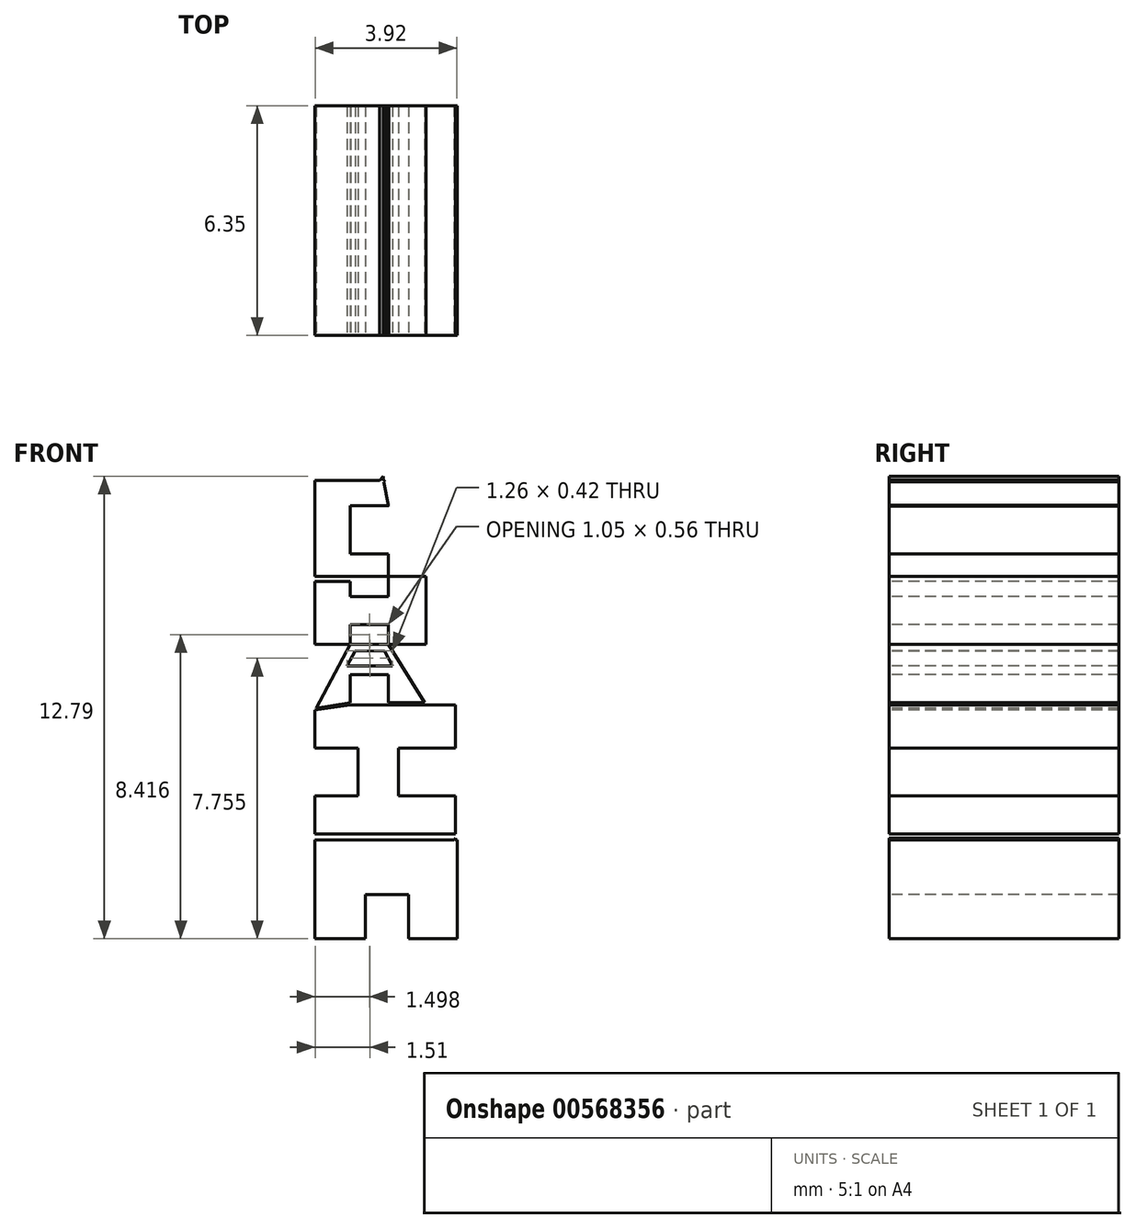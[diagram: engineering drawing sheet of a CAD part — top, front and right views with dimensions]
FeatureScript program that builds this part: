
annotation { "Feature Type Name" : "Feature", "Feature Type Description" : "" }
export const myFeature = defineFeature(function(context is Context, id is Id, definition is map)
    precondition{}
    {
        {
            var Q0;
            Q0=qCreatedBy(makeId("Front.planeOp"),FACE);
            var sketch = newSketch(context, id + "F0", { "sketchPlane" : qUnion([Q0])});
            skLineSegment(sketch, "E0", {"start": v(0, 0) * mm, "end": v(0, 25.4) * mm});
            skLineSegment(sketch, "E1", {"start": v(0, 25.4) * mm, "end": v(25.4, 25.4) * mm});
            skLineSegment(sketch, "E2", {"start": v(25.4, 25.4) * mm, "end": v(25.4, 0) * mm});
            skLineSegment(sketch, "E3", {"start": v(25.4, 0) * mm, "end": v(0, 0) * mm});
            skSolve(sketch);
        }
        {
            var Q0;
            Q0=makeQuery(id+"F0.imprint","IMPRINT",FACE,{"disambiguationData":[TD([[makeQuery(id+"F0.imprint","IMPRINT",EDGE,{"derivedFrom":sQuery(id+"F0.wireOp",EDGE,"E0")}),-1.0]])]});
            extrude(context, id + "F1", {"entities" : qUnion([Q0]), "depth" : 6.35 * mm, "offsetDistance" : 25.4 * mm});
        }
        {
            var Q0;
            Q0=makeQuery(id+"F1.opExtrude","CAP_FACE",FACE,{"disambiguationData":[OSD([sQuery(id+"F0.wireOp",EDGE,"E0"),sQuery(id+"F0.wireOp",EDGE,"E1"),sQuery(id+"F0.wireOp",EDGE,"E2"),sQuery(id+"F0.wireOp",EDGE,"E3")])],"isStart":false});
            var sketch = newSketch(context, id + "F2", { "sketchPlane" : qUnion([Q0])});
            skLineSegment(sketch, "E4", {"start": v(5.84, 25.4) * mm, "end": v(20.13, 25.4) * mm});
            skLineSegment(sketch, "E5", {"start": v(20.13, 25.4) * mm, "end": v(25.4, 21.86) * mm});
            skLineSegment(sketch, "E6", {"start": v(25.4, 21.86) * mm, "end": v(25.4, 16.78) * mm});
            skLineSegment(sketch, "E7", {"start": v(25.4, 16.78) * mm, "end": v(20.17, 13.18) * mm});
            skLineSegment(sketch, "E8", {"start": v(20.17, 13.18) * mm, "end": v(16.36, 13.18) * mm});
            skLineSegment(sketch, "E9", {"start": v(16.36, 13.18) * mm, "end": v(16.36, 1.75) * mm});
            skLineSegment(sketch, "E10", {"start": v(16.36, 1.75) * mm, "end": v(14.52, 0) * mm});
            skLineSegment(sketch, "E11", {"start": v(5.84, 25.4) * mm, "end": v(0, 22.9) * mm});
            skLineSegment(sketch, "E12", {"start": v(0, 22.9) * mm, "end": v(0, 17.82) * mm});
            skLineSegment(sketch, "E13", {"start": v(0, 17.82) * mm, "end": v(4.83, 13.7) * mm});
            skLineSegment(sketch, "E14", {"start": v(4.83, 13.7) * mm, "end": v(11.25, 13.7) * mm});
            skLineSegment(sketch, "E15", {"start": v(11.25, 13.7) * mm, "end": v(11.25, 12.68) * mm});
            skLineSegment(sketch, "E16", {"start": v(8.5, 23.69) * mm, "end": v(2.71, 21.07) * mm});
            skLineSegment(sketch, "E17", {"start": v(2.71, 21.07) * mm, "end": v(21.76, 21.07) * mm});
            skLineSegment(sketch, "E18", {"start": v(21.76, 21.07) * mm, "end": v(16.12, 23.97) * mm});
            skLineSegment(sketch, "E19", {"start": v(16.12, 23.97) * mm, "end": v(8.5, 23.69) * mm});
            skPoint(sketch, "E20.endSnap0", {"position": v(9.86, 17.7) * mm});
            skLineSegment(sketch, "E21", {"start": v(11.25, 12.68) * mm, "end": v(9.37, 12.68) * mm});
            skLineSegment(sketch, "E22", {"start": v(9.37, 12.68) * mm, "end": v(9.37, 10.02) * mm});
            skLineSegment(sketch, "E23", {"start": v(9.37, 10.02) * mm, "end": v(11.4, 10.02) * mm});
            skLineSegment(sketch, "E24", {"start": v(11.4, 10.02) * mm, "end": v(11.4, 10.65) * mm});
            skLineSegment(sketch, "E25", {"start": v(11.4, 10.65) * mm, "end": v(10.34, 10.65) * mm});
            skLineSegment(sketch, "E26", {"start": v(10.34, 10.65) * mm, "end": v(10.34, 11.98) * mm});
            skLineSegment(sketch, "E27", {"start": v(10.34, 11.98) * mm, "end": v(11.4, 11.98) * mm});
            skLineSegment(sketch, "E28", {"start": v(11.4, 11.98) * mm, "end": v(11.25, 12.68) * mm});
            skLineSegment(sketch, "E29", {"start": v(9.37, 8.14) * mm, "end": v(10.34, 8.14) * mm});
            skLineSegment(sketch, "E30", {"start": v(10.34, 8.14) * mm, "end": v(10.34, 8.7) * mm});
            skLineSegment(sketch, "E31", {"start": v(10.34, 8.7) * mm, "end": v(11.4, 8.7) * mm});
            skLineSegment(sketch, "E32", {"start": v(11.4, 8.7) * mm, "end": v(11.4, 8.14) * mm});
            skLineSegment(sketch, "E33", {"start": v(11.4, 8.14) * mm, "end": v(12.44, 8.14) * mm});
            skLineSegment(sketch, "E34", {"start": v(12.44, 8.14) * mm, "end": v(12.44, 10.02) * mm});
            skLineSegment(sketch, "E35", {"start": v(12.44, 10.02) * mm, "end": v(11.4, 10.02) * mm});
            skLineSegment(sketch, "E36", {"start": v(11.4, 10.02) * mm, "end": v(11.4, 9.46) * mm});
            skLineSegment(sketch, "E37", {"start": v(11.4, 9.46) * mm, "end": v(10.34, 9.46) * mm});
            skLineSegment(sketch, "E38", {"start": v(10.34, 9.46) * mm, "end": v(10.34, 10.02) * mm});
            skLineSegment(sketch, "E39", {"start": v(9.37, 6.32) * mm, "end": v(10.34, 8.14) * mm});
            skLineSegment(sketch, "E40", {"start": v(11.4, 8.14) * mm, "end": v(10.34, 8.14) * mm});
            skLineSegment(sketch, "E41", {"start": v(11.4, 8.14) * mm, "end": v(12.44, 6.46) * mm});
            skLineSegment(sketch, "E42", {"start": v(12.44, 6.46) * mm, "end": v(11.4, 6.46) * mm});
            skLineSegment(sketch, "E43", {"start": v(11.4, 6.46) * mm, "end": v(11.4, 7.3) * mm});
            skPoint(sketch, "E43.endSnap0", {"position": v(11.92, 7.3) * mm});
            skLineSegment(sketch, "E44", {"start": v(11.4, 7.3) * mm, "end": v(10.34, 7.3) * mm});
            skLineSegment(sketch, "E45", {"start": v(10.34, 7.3) * mm, "end": v(10.34, 6.46) * mm});
            skLineSegment(sketch, "E46", {"start": v(10.34, 6.46) * mm, "end": v(9.37, 6.32) * mm});
            skLineSegment(sketch, "E47", {"start": v(9.37, 6.32) * mm, "end": v(9.37, 5.27) * mm});
            skLineSegment(sketch, "E48", {"start": v(9.37, 5.27) * mm, "end": v(10.55, 5.27) * mm});
            skLineSegment(sketch, "E49", {"start": v(10.55, 5.27) * mm, "end": v(10.55, 3.95) * mm});
            skLineSegment(sketch, "E50", {"start": v(10.55, 3.95) * mm, "end": v(9.37, 3.95) * mm});
            skLineSegment(sketch, "E51", {"start": v(9.37, 3.95) * mm, "end": v(9.37, 2.9) * mm});
            skLineSegment(sketch, "E52", {"start": v(9.37, 2.9) * mm, "end": v(13.25, 2.9) * mm});
            skLineSegment(sketch, "E53", {"start": v(13.25, 2.9) * mm, "end": v(13.25, 3.95) * mm});
            skLineSegment(sketch, "E54", {"start": v(13.25, 3.95) * mm, "end": v(11.67, 3.95) * mm});
            skLineSegment(sketch, "E55", {"start": v(11.67, 3.95) * mm, "end": v(11.67, 5.27) * mm});
            skLineSegment(sketch, "E56", {"start": v(11.67, 5.27) * mm, "end": v(13.25, 5.27) * mm});
            skLineSegment(sketch, "E57", {"start": v(13.25, 5.27) * mm, "end": v(13.25, 6.46) * mm});
            skLineSegment(sketch, "E58", {"start": v(13.25, 6.46) * mm, "end": v(12.44, 6.46) * mm});
            skLineSegment(sketch, "E59", {"start": v(10.34, 6.46) * mm, "end": v(11.4, 6.46) * mm});
            skLineSegment(sketch, "E60", {"start": v(9.37, 0) * mm, "end": v(10.76, 0) * mm});
            skLineSegment(sketch, "E61", {"start": v(10.76, 0) * mm, "end": v(10.76, 1.22) * mm});
            skLineSegment(sketch, "E62", {"start": v(10.76, 1.22) * mm, "end": v(11.95, 1.22) * mm});
            skLineSegment(sketch, "E63", {"start": v(11.95, 1.22) * mm, "end": v(11.95, 0) * mm});
            skLineSegment(sketch, "E64", {"start": v(13.25, 2.9) * mm, "end": v(13.25, 0) * mm});
            skLineSegment(sketch, "E65", {"start": v(13.25, 0) * mm, "end": v(11.95, 0) * mm});
            skLineSegment(sketch, "E66", {"start": v(14.52, 0) * mm, "end": v(13.25, 0) * mm});
            skLineSegment(sketch, "E67", {"start": v(11.4, 11.98) * mm, "end": v(11.4, 10.65) * mm});
            skLineSegment(sketch, "E68", {"start": v(11.4, 10.65) * mm, "end": v(12.44, 10.02) * mm});
            skLineSegment(sketch, "E69", {"start": v(13.25, 5.27) * mm, "end": v(13.25, 3.95) * mm});
            skLineSegment(sketch, "E70", {"start": v(13.25, 6.46) * mm, "end": v(12.44, 8.14) * mm});
            skLineSegment(sketch, "E71", {"start": v(12.44, 10.02) * mm, "end": v(13.22, 10.02) * mm});
            skLineSegment(sketch, "E72", {"start": v(13.22, 10.02) * mm, "end": v(13.25, 6.46) * mm});
            skLineSegment(sketch, "E73", {"start": v(4.1, 19.7) * mm, "end": v(4.1, 16.53) * mm});
            skLineSegment(sketch, "E74", {"start": v(4.1, 16.53) * mm, "end": v(4.87, 16.53) * mm});
            skLineSegment(sketch, "E75", {"start": v(4.87, 16.53) * mm, "end": v(4.87, 17.65) * mm});
            skLineSegment(sketch, "E76", {"start": v(4.87, 17.65) * mm, "end": v(6.18, 16.45) * mm});
            skLineSegment(sketch, "E77", {"start": v(6.18, 16.45) * mm, "end": v(6.65, 17) * mm});
            skLineSegment(sketch, "E78", {"start": v(6.65, 17) * mm, "end": v(5.81, 17.74) * mm});
            skLineSegment(sketch, "E79", {"start": v(5.81, 17.74) * mm, "end": v(6.65, 18.7) * mm});
            skLineSegment(sketch, "E80", {"start": v(6.65, 18.7) * mm, "end": v(5.7, 19.52) * mm});
            skLineSegment(sketch, "E81", {"start": v(5.7, 19.52) * mm, "end": v(4.87, 18.57) * mm});
            skLineSegment(sketch, "E82", {"start": v(4.1, 19.7) * mm, "end": v(4.87, 19.7) * mm});
            skLineSegment(sketch, "E83", {"start": v(4.87, 19.7) * mm, "end": v(4.87, 18.57) * mm});
            skLineSegment(sketch, "E84", {"start": v(9.86, 17.7) * mm, "end": v(9.86, 19.59) * mm});
            skLineSegment(sketch, "E85", {"start": v(9.86, 19.59) * mm, "end": v(11.8, 19.59) * mm});
            skLineSegment(sketch, "E86", {"start": v(11.8, 19.59) * mm, "end": v(11.8, 18.83) * mm});
            skLineSegment(sketch, "E87", {"start": v(11.8, 18.83) * mm, "end": v(10.53, 18.83) * mm});
            skLineSegment(sketch, "E88", {"start": v(10.53, 18.83) * mm, "end": v(10.53, 18.07) * mm});
            skLineSegment(sketch, "E89", {"start": v(10.53, 18.07) * mm, "end": v(11.1, 18.07) * mm});
            skLineSegment(sketch, "E90", {"start": v(11.1, 18.07) * mm, "end": v(11.1, 16.8) * mm});
            skLineSegment(sketch, "E91", {"start": v(11.1, 16.8) * mm, "end": v(10.56, 16.8) * mm});
            skLineSegment(sketch, "E92", {"start": v(10.56, 16.8) * mm, "end": v(10.56, 16.04) * mm});
            skLineSegment(sketch, "E93", {"start": v(10.56, 16.04) * mm, "end": v(11.83, 16.04) * mm});
            skLineSegment(sketch, "E94", {"start": v(11.83, 16.04) * mm, "end": v(11.83, 15.28) * mm});
            skLineSegment(sketch, "E95", {"start": v(11.83, 15.28) * mm, "end": v(9.86, 15.28) * mm});
            skLineSegment(sketch, "E96", {"start": v(9.86, 15.28) * mm, "end": v(9.86, 17.7) * mm});
            skLineSegment(sketch, "E97", {"start": v(16.72, 19.59) * mm, "end": v(18.3, 17.55) * mm});
            skPoint(sketch, "E97.startSnap0", {"position": v(10.83, 19.59) * mm});
            skLineSegment(sketch, "E98", {"start": v(18.3, 17.55) * mm, "end": v(16.12, 15.42) * mm});
            skLineSegment(sketch, "E99", {"start": v(16.12, 15.42) * mm, "end": v(16.77, 14.76) * mm});
            skLineSegment(sketch, "E100", {"start": v(16.77, 14.76) * mm, "end": v(21.31, 19.2) * mm});
            skLineSegment(sketch, "E101", {"start": v(21.31, 19.2) * mm, "end": v(20.82, 19.65) * mm});
            skLineSegment(sketch, "E102", {"start": v(20.82, 19.65) * mm, "end": v(18.8, 18.11) * mm});
            skLineSegment(sketch, "E103", {"start": v(18.8, 18.11) * mm, "end": v(17.35, 20.02) * mm});
            skLineSegment(sketch, "E104", {"start": v(17.35, 20.02) * mm, "end": v(16.72, 19.59) * mm});
            skLineSegment(sketch, "E105", {"start": v(11.4, 10.64) * mm, "end": v(11.4, 10.65) * mm});
            skLineSegment(sketch, "E106", {"start": v(11.4, 10.02) * mm, "end": v(11.4, 10.02) * mm});
            skLineSegment(sketch, "E107", {"start": v(12.44, 10.02) * mm, "end": v(12.43, 10.02) * mm});
            skLineSegment(sketch, "E108", {"start": v(10.34, 8.15) * mm, "end": v(10.35, 8.14) * mm});
            skLineSegment(sketch, "E109", {"start": v(11.38, 8.14) * mm, "end": v(11.4, 8.15) * mm});
            skLineSegment(sketch, "E110", {"start": v(9.37, 2.73) * mm, "end": v(13.25, 2.73) * mm});
            skLineSegment(sketch, "E111", {"start": v(13.25, 2.73) * mm, "end": v(13.25, 2.9) * mm});
            skLineSegment(sketch, "E112", {"start": v(13.25, 2.9) * mm, "end": v(9.37, 2.9) * mm});
            skPoint(sketch, "E113.centerSnap0", {"position": v(18.94, 22.52) * mm});
            skLineSegment(sketch, "E114", {"start": v(11.25, 12.68) * mm, "end": v(11.36, 12.7) * mm});
            skLineSegment(sketch, "E115", {"start": v(11.36, 12.7) * mm, "end": v(11.5, 12) * mm});
            skLineSegment(sketch, "E116", {"start": v(11.5, 12) * mm, "end": v(11.4, 11.98) * mm});
            skLineSegment(sketch, "E117", {"start": v(10.34, 10.02) * mm, "end": v(10.34, 9.88) * mm});
            skLineSegment(sketch, "E118", {"start": v(10.34, 9.88) * mm, "end": v(9.37, 9.88) * mm});
            skLineSegment(sketch, "E119", {"start": v(10.34, 10.02) * mm, "end": v(9.37, 10.02) * mm});
            skLineSegment(sketch, "E120", {"start": v(11.4, 6.46) * mm, "end": v(11.4, 6.53) * mm});
            skLineSegment(sketch, "E121", {"start": v(11.4, 6.53) * mm, "end": v(12.4, 6.53) * mm});
            skLineSegment(sketch, "E122", {"start": v(12.4, 6.53) * mm, "end": v(12.44, 6.46) * mm});
            skLineSegment(sketch, "E123", {"start": v(10.34, 6.46) * mm, "end": v(10.34, 6.53) * mm});
            skLineSegment(sketch, "E124", {"start": v(10.34, 6.53) * mm, "end": v(9.4, 6.38) * mm});
            skLineSegment(sketch, "E125", {"start": v(9.4, 6.38) * mm, "end": v(9.37, 6.32) * mm});
            skLineSegment(sketch, "E126", {"start": v(11.15, 12.68) * mm, "end": v(11.25, 12.79) * mm});
            skLineSegment(sketch, "E127", {"start": v(11.25, 12.79) * mm, "end": v(11.25, 12.68) * mm});
            skLineSegment(sketch, "E128", {"start": v(11.3, 12.69) * mm, "end": v(11.26, 12.64) * mm});
            skLineSegment(sketch, "E129", {"start": v(9.37, 2.73) * mm, "end": v(9.37, 0) * mm});
            skLineSegment(sketch, "E130", {"start": v(9.37, 9.88) * mm, "end": v(9.37, 8.14) * mm});
            skLineSegment(sketch, "E131", {"start": v(11.38, 11.98) * mm, "end": v(11.4, 11.96) * mm});
            skLineSegment(sketch, "E132", {"start": v(11.39, 12) * mm, "end": v(11.4, 11.98) * mm});
            skLineSegment(sketch, "E133", {"start": v(10.47, 7.96) * mm, "end": v(10.25, 7.55) * mm});
            skLineSegment(sketch, "E134", {"start": v(10.25, 7.55) * mm, "end": v(11.51, 7.55) * mm});
            skLineSegment(sketch, "E135", {"start": v(11.51, 7.55) * mm, "end": v(11.3, 7.96) * mm});
            skLineSegment(sketch, "E136", {"start": v(11.3, 7.96) * mm, "end": v(10.47, 7.96) * mm});
            skLineSegment(sketch, "E137", {"start": v(13.2, 2.73) * mm, "end": v(13.25, 2.78) * mm});
            skLineSegment(sketch, "E138", {"start": v(13.25, 2.73) * mm, "end": v(13.3, 2.73) * mm});
            skLineSegment(sketch, "E139", {"start": v(13.3, 2.73) * mm, "end": v(13.3, 0) * mm});
            skLineSegment(sketch, "E140", {"start": v(13.3, 0) * mm, "end": v(13.25, 0) * mm});
            skLineSegment(sketch, "E141", {"start": v(13.25, 0) * mm, "end": v(13.3, 0) * mm});
            skSolve(sketch);
        }
        {
            var Q0;
            {var subQ1=sQuery(id+"F2.wireOp",EDGE,"E115");Q0=makeQuery(id+"F2.imprint","IMPRINT",FACE,{"disambiguationData":[TD([[makeQuery(id+"F2.imprint","IMPRINT",EDGE,{"derivedFrom":subQ1}),-1.0]])]});}
            extrude(context, id + "F3", {"entities" : qUnion([Q0]), "operationType" : NewBodyOperationType.REMOVE, "oppositeDirection" : true, "depth" : 25.4 * mm, "offsetDistance" : 25.4 * mm});
        }
        {
            var Q0;
            Q0=makeQuery(id+"F2.imprint","IMPRINT",FACE,{"disambiguationData":[TD([[makeQuery(id+"F2.imprint","IMPRINT",EDGE,{"derivedFrom":sQuery(id+"F2.wireOp",EDGE,"E73")}),1.0]])]});
            var Q1;
            Q1=makeQuery(id+"F2.imprint","IMPRINT",FACE,{"disambiguationData":[TD([[makeQuery(id+"F2.imprint","IMPRINT",EDGE,{"derivedFrom":sQuery(id+"F2.wireOp",EDGE,"E97")}),1.0]])]});
            var Q2;
            Q2=makeQuery(id+"F2.imprint","IMPRINT",FACE,{"disambiguationData":[TD([[makeQuery(id+"F2.imprint","IMPRINT",EDGE,{"derivedFrom":sQuery(id+"F2.wireOp",EDGE,"E84")}),-1.0]])]});
            extrude(context, id + "F4", {"entities" : qUnion([Q0, Q1, Q2]), "operationType" : NewBodyOperationType.REMOVE, "oppositeDirection" : true, "depth" : 25.4 * mm, "offsetDistance" : 25.4 * mm});
        }
        {
            var Q0;
            Q0=makeQuery(id+"F2.imprint","IMPRINT",FACE,{"disambiguationData":[TD([[makeQuery(id+"F2.imprint","IMPRINT",EDGE,{"derivedFrom":sQuery(id+"F2.wireOp",EDGE,"E25")}),-1.0]])]});
            var Q1;
            Q1=makeQuery(id+"F2.imprint","IMPRINT",FACE,{"disambiguationData":[TD([[makeQuery(id+"F2.imprint","IMPRINT",EDGE,{"derivedFrom":sQuery(id+"F2.wireOp",EDGE,"E43")}),1.0]])]});
            var Q2;
            Q2=makeQuery(id+"F2.imprint","IMPRINT",FACE,{"disambiguationData":[TD([[makeQuery(id+"F2.imprint","IMPRINT",EDGE,{"derivedFrom":sQuery(id+"F2.wireOp",EDGE,"E54")}),-1.0]])]});
            var Q3;
            {var subQ0=sQuery(id+"F2.wireOp",EDGE,"E61");Q3=makeQuery(id+"F2.imprint","IMPRINT",FACE,{"disambiguationData":[TD([[makeQuery(id+"F2.imprint","IMPRINT",EDGE,{"derivedFrom":subQ0}),-1.0]])]});}
            var Q4;
            {var subQ0=sQuery(id+"F2.wireOp",EDGE,"E36");Q4=makeQuery(id+"F2.imprint","IMPRINT",FACE,{"disambiguationData":[TD([[makeQuery(id+"F2.imprint","IMPRINT",EDGE,{"derivedFrom":subQ0}),-1.0]])]});}
            extrude(context, id + "F5", {"entities" : qUnion([Q0, Q1, Q2, Q3, Q4]), "operationType" : NewBodyOperationType.REMOVE, "oppositeDirection" : true, "depth" : 25.4 * mm, "offsetDistance" : 25.4 * mm});
        }
        {
            var Q0;
            Q0=makeQuery(id+"F2.imprint","IMPRINT",FACE,{"disambiguationData":[TD([[makeQuery(id+"F2.imprint","IMPRINT",EDGE,{"derivedFrom":sQuery(id+"F2.wireOp",EDGE,"E33")}),-1.0]])]});
            var Q1;
            Q1=makeQuery(id+"F2.imprint","IMPRINT",FACE,{"disambiguationData":[TD([[makeQuery(id+"F2.imprint","IMPRINT",EDGE,{"derivedFrom":sQuery(id+"F2.wireOp",EDGE,"E34")}),-1.0]])]});
            extrude(context, id + "F6", {"entities" : qUnion([Q0, Q1]), "operationType" : NewBodyOperationType.REMOVE, "oppositeDirection" : true, "depth" : 25.4 * mm, "offsetDistance" : 25.4 * mm});
        }
        {
            var Q0;
            {var subQ4=sQuery(id+"F2.wireOp",EDGE,"E31");Q0=makeQuery(id+"F2.imprint","IMPRINT",FACE,{"disambiguationData":[TD([[makeQuery(id+"F2.imprint","IMPRINT",EDGE,{"derivedFrom":subQ4}),-1.0]])]});}
            var Q1;
            {var subQ0=sQuery(id+"F2.wireOp",EDGE,"E105");Q1=makeQuery(id+"F2.imprint","IMPRINT",FACE,{"disambiguationData":[TD([[makeQuery(id+"F2.imprint","IMPRINT",EDGE,{"derivedFrom":subQ0}),-1.0]])]});}
            extrude(context, id + "F7", {"entities" : qUnion([Q0, Q1]), "operationType" : NewBodyOperationType.REMOVE, "oppositeDirection" : true, "depth" : 25.4 * mm, "offsetDistance" : 25.4 * mm});
        }
        {
            var Q0;
            {var subQ0=sQuery(id+"F2.wireOp",EDGE,"E11");Q0=makeQuery(id+"F2.imprint","IMPRINT",FACE,{"disambiguationData":[TD([[makeQuery(id+"F2.imprint","IMPRINT",EDGE,{"derivedFrom":subQ0}),-1.0]])]});}
            var Q1;
            {var subQ0=sQuery(id+"F2.wireOp",EDGE,"E5");Q1=makeQuery(id+"F2.imprint","IMPRINT",FACE,{"disambiguationData":[TD([[makeQuery(id+"F2.imprint","IMPRINT",EDGE,{"derivedFrom":subQ0}),1.0]])]});}
            var Q2;
            {var subQ4=sQuery(id+"F2.wireOp",EDGE,"E13");Q2=makeQuery(id+"F2.imprint","IMPRINT",FACE,{"disambiguationData":[TD([[makeQuery(id+"F2.imprint","IMPRINT",EDGE,{"derivedFrom":subQ4}),-1.0]])]});}
            var Q3;
            Q3=makeQuery(id+"F2.imprint","IMPRINT",FACE,{"disambiguationData":[TD([[makeQuery(id+"F2.imprint","IMPRINT",EDGE,{"derivedFrom":sQuery(id+"F2.wireOp",EDGE,"E16")}),1.0]])]});
            var Q4;
            {var subQ4=sQuery(id+"F2.wireOp",EDGE,"E7");Q4=makeQuery(id+"F2.imprint","IMPRINT",FACE,{"disambiguationData":[TD([[makeQuery(id+"F2.imprint","IMPRINT",EDGE,{"derivedFrom":subQ4}),1.0]])]});}
            extrude(context, id + "F8", {"entities" : qUnion([Q0, Q1, Q2, Q3, Q4]), "operationType" : NewBodyOperationType.REMOVE, "oppositeDirection" : true, "depth" : 25.4 * mm, "offsetDistance" : 25.4 * mm});
        }
        {
            var Q0;
            Q0=makeQuery(id+"F2.imprint","IMPRINT",FACE,{"disambiguationData":[TD([[makeQuery(id+"F2.imprint","IMPRINT",EDGE,{"derivedFrom":sQuery(id+"F2.wireOp",EDGE,"E46")}),-1.0]])]});
            var Q1;
            Q1=makeQuery(id+"F2.imprint","IMPRINT",FACE,{"disambiguationData":[TD([[makeQuery(id+"F2.imprint","IMPRINT",EDGE,{"derivedFrom":sQuery(id+"F2.wireOp",EDGE,"E42")}),-1.0]])]});
            extrude(context, id + "F9", {"entities" : qUnion([Q0, Q1]), "operationType" : NewBodyOperationType.REMOVE, "oppositeDirection" : true, "depth" : 25.4 * mm, "offsetDistance" : 25.4 * mm});
        }
        {
            var Q0;
            Q0=makeQuery(id+"F2.imprint","IMPRINT",FACE,{"disambiguationData":[TD([[makeQuery(id+"F2.imprint","IMPRINT",EDGE,{"derivedFrom":sQuery(id+"F2.wireOp",EDGE,"E133")}),1.0]])]});
            extrude(context, id + "F10", {"entities" : qUnion([Q0]), "operationType" : NewBodyOperationType.REMOVE, "oppositeDirection" : true, "depth" : 25.4 * mm, "offsetDistance" : 25.4 * mm});
        }
        {
            var Q0;
            Q0=makeQuery(id+"F2.imprint","IMPRINT",FACE,{"disambiguationData":[TD([[makeQuery(id+"F2.imprint","IMPRINT",EDGE,{"derivedFrom":sQuery(id+"F2.wireOp",EDGE,"E64")}),1.0]])]});
            extrude(context, id + "F11", {"entities" : qUnion([Q0]), "operationType" : NewBodyOperationType.REMOVE, "oppositeDirection" : true, "depth" : 25.4 * mm, "offsetDistance" : 25.4 * mm});
        }
    });
